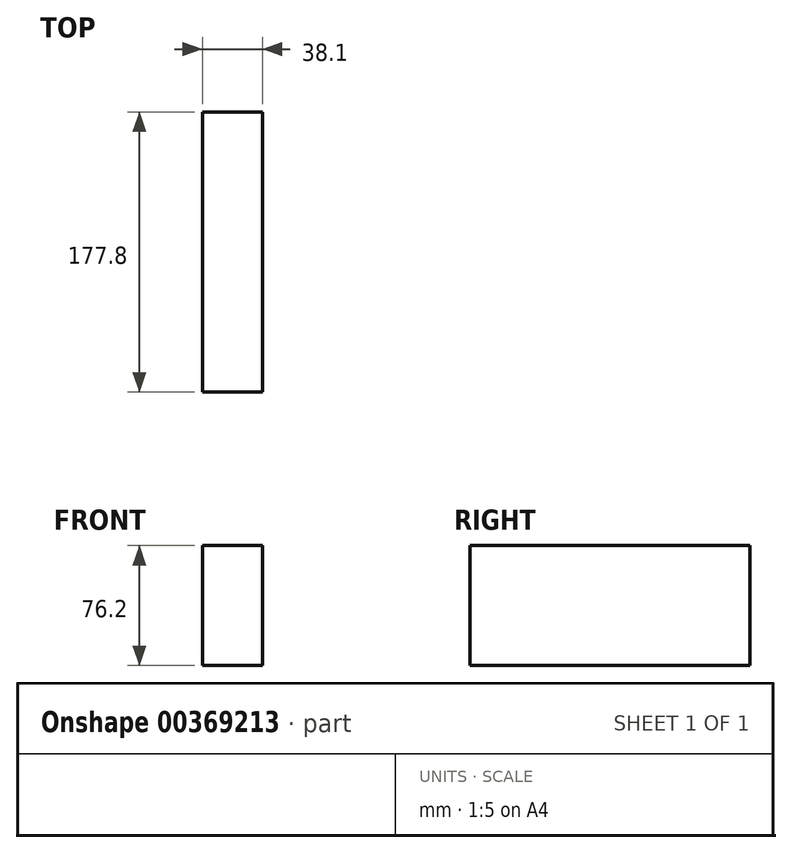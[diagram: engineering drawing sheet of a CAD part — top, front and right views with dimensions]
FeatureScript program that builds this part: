
annotation { "Feature Type Name" : "Feature", "Feature Type Description" : "" }
export const myFeature = defineFeature(function(context is Context, id is Id, definition is map)
    precondition{}
    {
        {
            var Q0;
            Q0=qCreatedBy(makeId("Top.planeOp"),FACE);
            var sketch = newSketch(context, id + "F0", { "sketchPlane" : qUnion([Q0])});
            skLineSegment(sketch, "E0.bottom", {"start": v(-417.91, -23.91) * mm, "end": v(-379.81, -23.91) * mm});
            skLineSegment(sketch, "E0.top", {"start": v(-417.91, -201.71) * mm, "end": v(-379.81, -201.71) * mm});
            skLineSegment(sketch, "E0.left", {"start": v(-417.91, -23.91) * mm, "end": v(-417.91, -201.71) * mm});
            skLineSegment(sketch, "E0.right", {"start": v(-379.81, -23.91) * mm, "end": v(-379.81, -201.71) * mm});
            skSolve(sketch);
        }
        {
            var Q0;
            Q0=makeQuery(id+"F0.imprint","IMPRINT",FACE,{"disambiguationData":[TD([[makeQuery(id+"F0.imprint","IMPRINT",EDGE,{"derivedFrom":sQuery(id+"F0.wireOp",EDGE,"E0.bottom")}),-1.0]])]});
            extrude(context, id + "F1", {"entities" : qUnion([Q0]), "depth" : 76.2 * mm});
        }
    });
